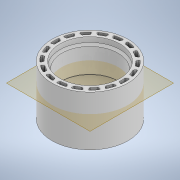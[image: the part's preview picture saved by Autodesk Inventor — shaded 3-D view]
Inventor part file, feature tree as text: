
AUTODESK INVENTOR PART (.ipt)
format: ipt  version: 2020 (Build 240168000, 168)  size: 279,040 bytes
history: native  units: mm
features: extrude x3, sketch x3, plane x1, chamfer x1, fillet x1, pattern_circular x1
ambient origin geometry x8: Origin, YZ Plane, XZ Plane, XY Plane, X Axis, Y Axis, Z Axis, Center Point
bodies: Solid1 (feature_tree)
feature tree (10):
  extrude  "Extrusion1"  Depth=30.0mm
  plane  "Work Plane1"
  extrude  "Extrusion2"  [1 undecoded]
  chamfer  "Chamfer1"  Distance=7.0mm
  extrude  "Extrusion3"  Depth=0.4mm TaperAngle=45.0deg
  fillet  "Fillet1"  [1 undecoded]
  pattern_circular  "Circular Pattern1"  Angle=30.0deg  [1 undecoded]
  sketch  "Sketch1"  dims[d0=38.0mm d1=30.0mm]
  sketch  "Sketch2"  dims[d2=25.0mm d3=0.0mm d4=-9.5mm]
  sketch  "Sketch3"  dims[d5=28.0mm d6=7.0mm d7=7.0mm d8=0.0mm d9=0.0mm d10=1.0mm d11=2.0mm d12=45.0deg d15=30.0deg d16=30.0deg d17=1.2mm d18=1.2mm d19=3.0mm d20=1.5mm d21=0.0mm d22=25.0mm d23=0.0mm d24=0.4mm d25=180.0mm d26=360.0deg]
note: 3 required parameter values undecoded (feature->parameter linkage not recoverable at this tier; creation-order binding heuristic only, values carry confidence <= 0.55)
